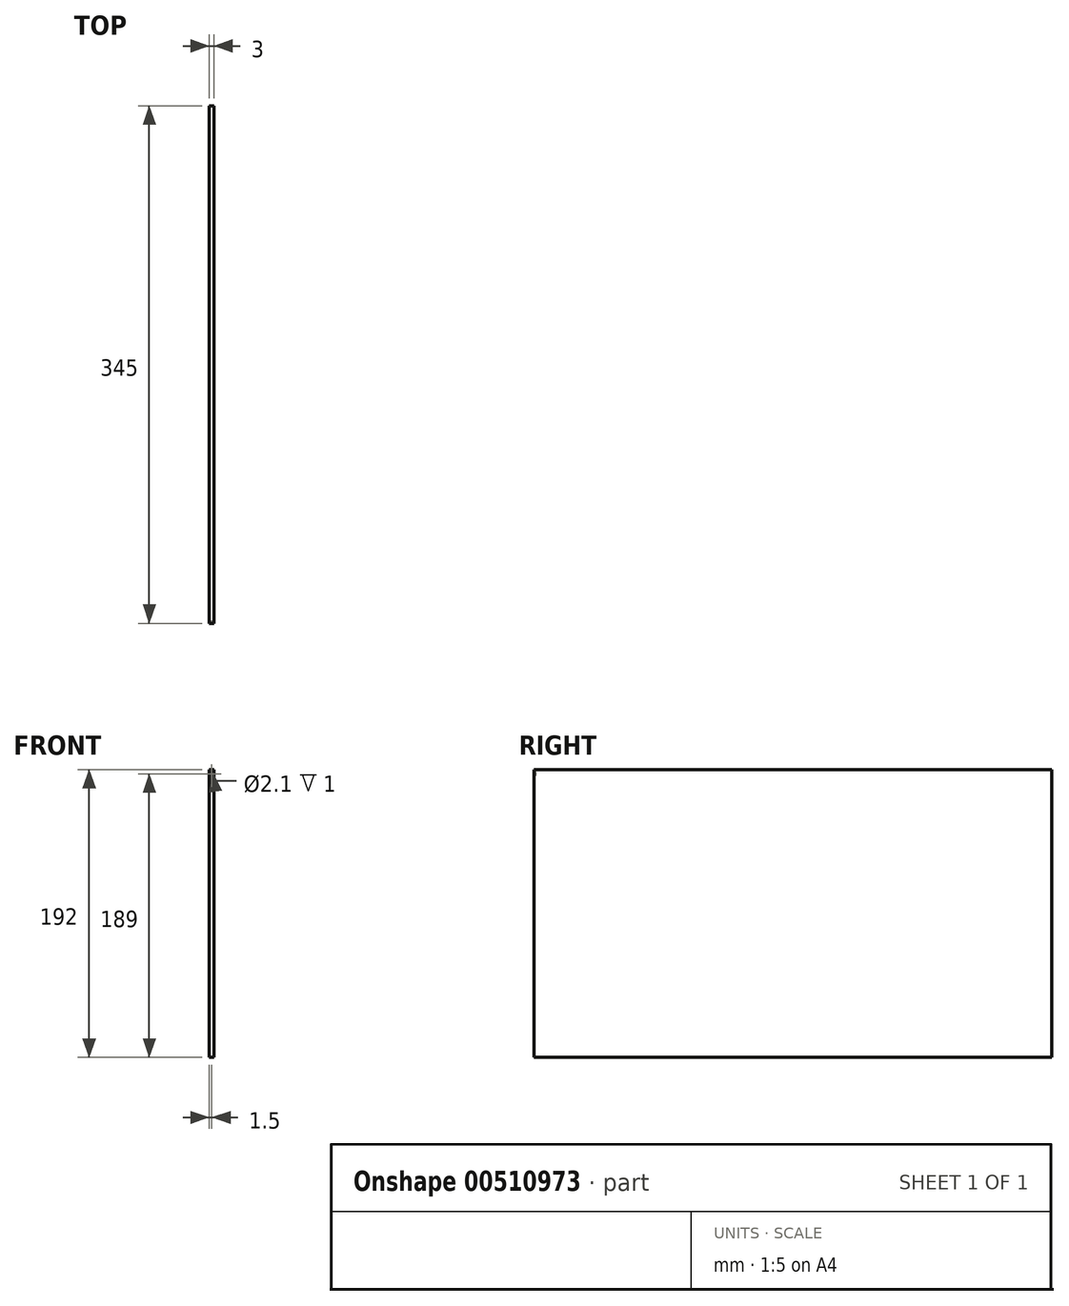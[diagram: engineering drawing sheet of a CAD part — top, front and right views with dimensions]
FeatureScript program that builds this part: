
annotation { "Feature Type Name" : "Feature", "Feature Type Description" : "" }
export const myFeature = defineFeature(function(context is Context, id is Id, definition is map)
    precondition{}
    {
        {
            var Q0;
            Q0=qCreatedBy(makeId("Right.planeOp"),FACE);
            var sketch = newSketch(context, id + "F0", { "sketchPlane" : qUnion([Q0])});
            skLineSegment(sketch, "E0.bottom", {"start": v(-172.5, 96) * mm, "end": v(172.5, 96) * mm});
            skLineSegment(sketch, "E0.top", {"start": v(-172.5, -96) * mm, "end": v(172.5, -96) * mm});
            skLineSegment(sketch, "E0.left", {"start": v(-172.5, 96) * mm, "end": v(-172.5, -96) * mm});
            skLineSegment(sketch, "E0.right", {"start": v(172.5, 96) * mm, "end": v(172.5, -96) * mm});
            skPoint(sketch, "E0.middle", {"position": v(0, 0) * mm});
            skSolve(sketch);
        }
        {
            var Q0;
            Q0=makeQuery(id+"F0.imprint","IMPRINT",FACE,{"disambiguationData":[TD([[makeQuery(id+"F0.imprint","IMPRINT",EDGE,{"derivedFrom":sQuery(id+"F0.wireOp",EDGE,"E0.bottom")}),-1.0]])]});
            extrude(context, id + "F1", {"entities" : qUnion([Q0]), "depth" : 3 * mm, "offsetDistance" : 25 * mm});
        }
        {
            var Q0;
            Q0=makeQuery(id+"F1.opExtrude","SWEPT_FACE",FACE,{"disambiguationData":[OSD([sQuery(id+"F0.wireOp",EDGE,"E0.left")])]});
            var sketch = newSketch(context, id + "F2", { "sketchPlane" : qUnion([Q0])});
            skLineSegment(sketch, "E1", {"start": v(1.5, 96) * mm, "end": v(1.5, 93) * mm});
            skCircle(sketch, "E2", {"center": v(1.5, 93) * mm, "radius": 1.05 * mm});
            skSolve(sketch);
        }
        {
            var Q0;
            Q0=makeQuery(id+"F2.imprint","IMPRINT",FACE,{"disambiguationData":[TD([[makeQuery(id+"F2.imprint","IMPRINT",EDGE,{"derivedFrom":sQuery(id+"F2.wireOp",EDGE,"E2")}),1.0]])]});
            extrude(context, id + "F3", {"entities" : qUnion([Q0]), "operationType" : NewBodyOperationType.REMOVE, "oppositeDirection" : true, "depth" : 1 * mm, "offsetDistance" : 25 * mm});
        }
    });
